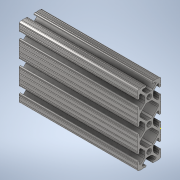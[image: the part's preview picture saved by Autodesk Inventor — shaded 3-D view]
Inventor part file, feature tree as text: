
AUTODESK INVENTOR PART (.ipt)
format: ipt  version: 2020 (Build 240168000, 168)  size: 373,248 bytes
history: native  units: in
note: dims shown in document units (in); Inventor stores cm internally (conversion verified against a paired STEP export)
features: sketch x2, extrude x1
ambient origin geometry x8: Origin, YZ Plane, XZ Plane, XY Plane, X Axis, Y Axis, Z Axis, Center Point
bodies: Solid1 (feature_tree)
feature tree (3):
  extrude  "Extrusion1"  [1 undecoded]
  sketch  "Sketch2"
  sketch  "Sketch1"  dims[d0=5.0in d1=0.0in]
note: 1 required parameter value undecoded (feature->parameter linkage not recoverable at this tier; creation-order binding heuristic only, values carry confidence <= 0.55)
